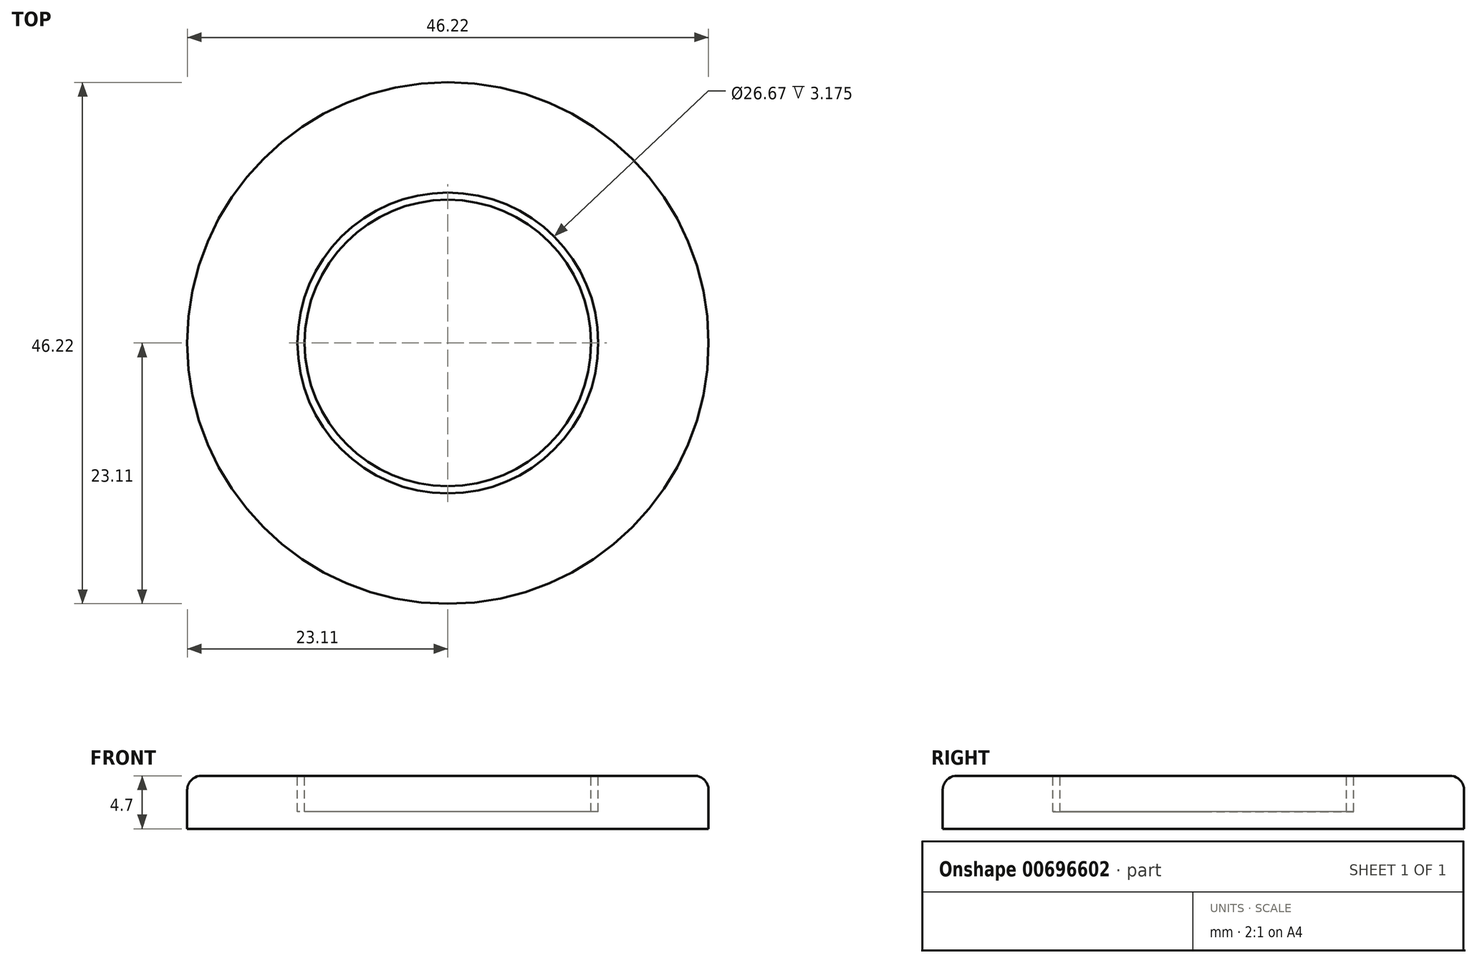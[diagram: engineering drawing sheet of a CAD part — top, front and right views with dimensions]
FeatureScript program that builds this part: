
annotation { "Feature Type Name" : "Feature", "Feature Type Description" : "" }
export const myFeature = defineFeature(function(context is Context, id is Id, definition is map)
    precondition{}
    {
        {
            var Q0;
            Q0=qCreatedBy(makeId("Top.planeOp"),FACE);
            var sketch = newSketch(context, id + "F0", { "sketchPlane" : qUnion([Q0])});
            skCircle(sketch, "E0", {"center": v(0, 0) * mm, "radius": 23.11 * mm});
            skSolve(sketch);
        }
        {
            var Q0;
            Q0 = qSketchRegion(id + "F0", true);
            extrude(context, id + "F1", {"entities" : qUnion([Q0]), "oppositeDirection" : true, "depth" : 4.7 * mm, "offsetDistance" : 25.4 * mm});
        }
        {
            var Q0;
            Q0=makeQuery(id+"F1.opExtrude","CAP_EDGE",EDGE,{"disambiguationData":[OSD([sQuery(id+"F0.wireOp",EDGE,"E0")])],"isStart":true});
            fillet(context, id + "F2", {"entities" : qUnion([Q0]), "radius" : 1.27 * mm, "tangentPropagation" : true, "allowEdgeOverflow" : false});
        }
        {
            var Q0;
            Q0=makeQuery(id+"F1.opExtrude","CAP_FACE",FACE,{"disambiguationData":[OSD([sQuery(id+"F0.wireOp",EDGE,"E0")])],"isStart":true});
            var sketch = newSketch(context, id + "F3", { "sketchPlane" : qUnion([Q0])});
            skCircle(sketch, "E1", {"center": v(0, 0) * mm, "radius": 13.34 * mm});
            skCircle(sketch, "E2", {"center": v(0, 0) * mm, "radius": 12.7 * mm});
            skSolve(sketch);
        }
        {
            var Q0;
            Q0 = qSketchRegion(id + "F3", true);
            extrude(context, id + "F4", {"entities" : qUnion([Q0]), "operationType" : NewBodyOperationType.REMOVE, "oppositeDirection" : true, "depth" : 3.17 * mm, "offsetDistance" : 25.4 * mm});
        }
    });
